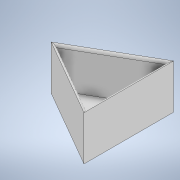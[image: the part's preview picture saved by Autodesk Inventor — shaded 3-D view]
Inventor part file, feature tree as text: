
AUTODESK INVENTOR PART (.ipt)
format: ipt  version: 2020.3 (Build 243373000, 373)  size: 128,512 bytes
history: native  units: mm
features: extrude x5, sketch x5, fillet x1
ambient origin geometry x8: Origin, YZ Plane, XZ Plane, XY Plane, X Axis, Y Axis, Z Axis, Center Point
bodies: Solid1 (feature_tree)
feature tree (11):
  extrude  "Extrusion1"  Depth=5.0mm
  extrude  "Extrusion3"  Depth=5.0mm
  extrude  "Extrusion4"  TaperAngle=0.0deg  [1 undecoded]
  extrude  "Extrusion5"  Depth=2.5mm
  extrude  "Extrusion6"  Depth=2.5mm
  fillet  "Fillet1"  Radius=0.5mm
  sketch  "Sketch1"  dims[d3=5.0mm d4=0.0mm d9=8.5mm]
  sketch  "Sketch5"  dims[d10=2.0mm d11=0.0mm d12=5.0mm]
  sketch  "Sketch6"  dims[d13=10.0mm d14=0.0mm d15=0.0mm d16=0.0mm]
  sketch  "Sketch7"  dims[d17=2.5mm d18=2.5mm]
  sketch  "Sketch8"  dims[d19=40.0mm d20=0.0mm d21=2.5mm d7=0.5mm d8=0.872665mm]
note: 1 required parameter value undecoded (feature->parameter linkage not recoverable at this tier; creation-order binding heuristic only, values carry confidence <= 0.55)
